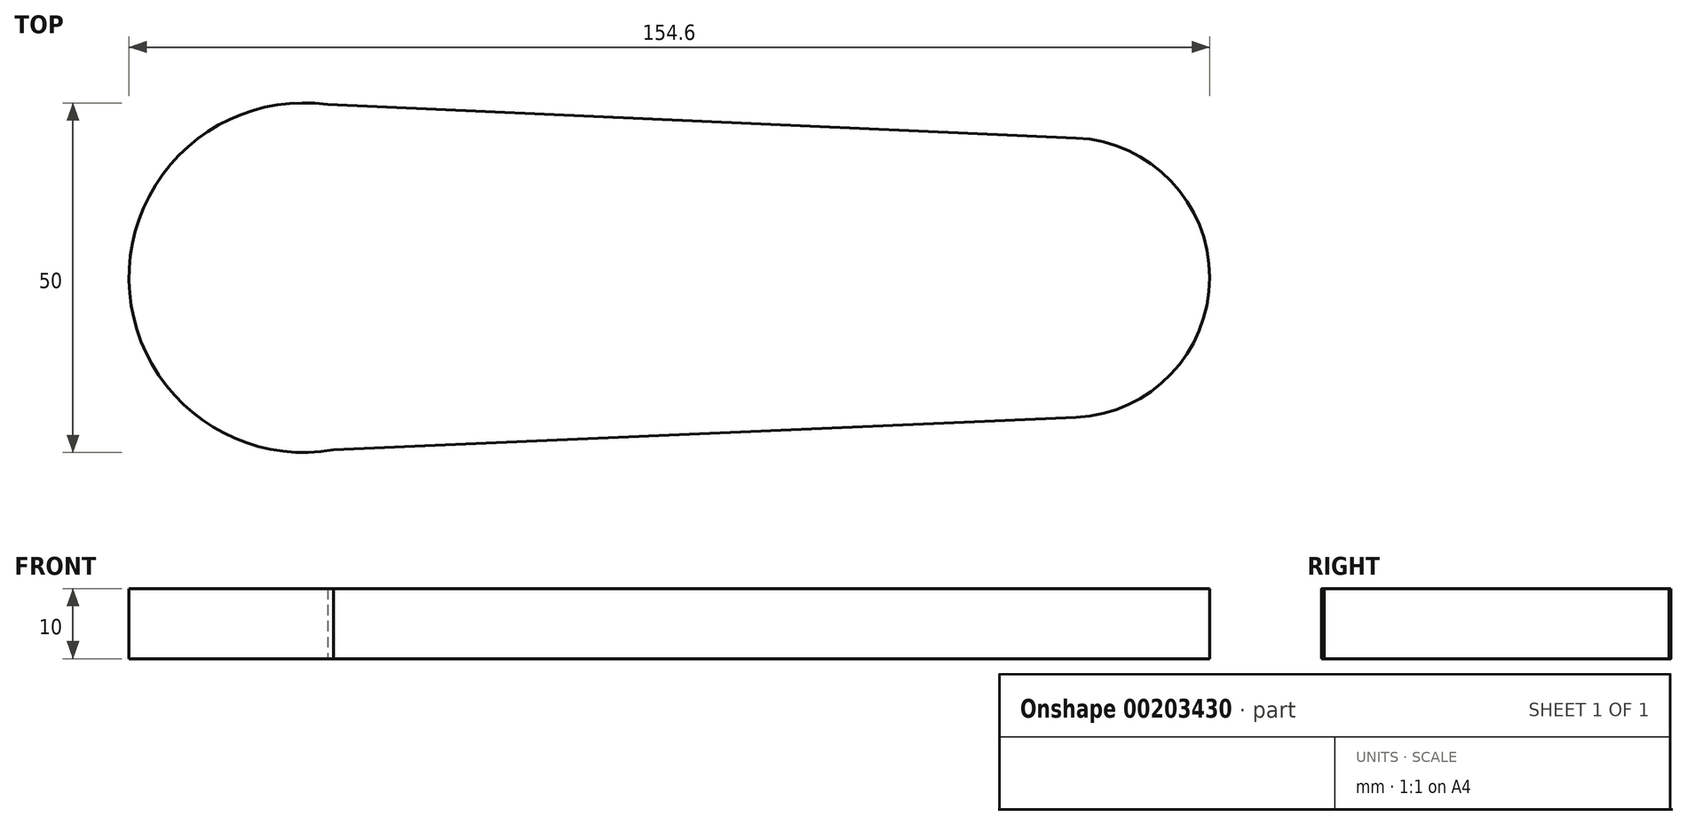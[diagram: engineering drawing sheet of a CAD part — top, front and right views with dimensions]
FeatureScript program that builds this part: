
annotation { "Feature Type Name" : "Feature", "Feature Type Description" : "" }
export const myFeature = defineFeature(function(context is Context, id is Id, definition is map)
    precondition{}
    {
        {
            var Q0;
            Q0=qCreatedBy(makeId("Top.planeOp"),FACE);
            var sketch = newSketch(context, id + "F0", { "sketchPlane" : qUnion([Q0])});
            skCircle(sketch, "E0", {"center": v(0, 0) * mm, "radius": 25 * mm});
            skCircle(sketch, "E1", {"center": v(109.6, 0) * mm, "radius": 20 * mm});
            skLineSegment(sketch, "E2", {"start": v(0, 0) * mm, "end": v(109.6, 0) * mm});
            skLineSegment(sketch, "E3", {"start": v(3.44, 24.76) * mm, "end": v(110.5, 19.98) * mm});
            skLineSegment(sketch, "E4", {"start": v(4.27, -24.63) * mm, "end": v(110.48, -19.98) * mm});
            skSolve(sketch);
        }
        {
            var Q0;
            {var subQ0=sQuery(id+"F0.wireOp",EDGE,"E0");var subQ1=makeQuery(id+"F0.imprint","INTERSECT",VERTEX,{"derivedFrom":[subQ0,sQuery(id+"F0.wireOp",EDGE,"E3")]});Q0=makeQuery(id+"F0.imprint","IMPRINT",FACE,{"disambiguationData":[TD([[makeQuery(id+"F0.imprint","IMPRINT",EDGE,{"disambiguationData":[TD([[subQ1,1.0]])],"derivedFrom":subQ0}),1.0]])]});}
            var Q1;
            {var subQ0=sQuery(id+"F0.wireOp",EDGE,"E1");var subQ1=makeQuery(id+"F0.imprint","INTERSECT",VERTEX,{"derivedFrom":[subQ0,sQuery(id+"F0.wireOp",EDGE,"E3")]});Q1=makeQuery(id+"F0.imprint","IMPRINT",FACE,{"disambiguationData":[TD([[makeQuery(id+"F0.imprint","IMPRINT",EDGE,{"disambiguationData":[TD([[subQ1,-1.0]])],"derivedFrom":subQ0}),1.0]])]});}
            var Q2;
            {var subQ0=sQuery(id+"F0.wireOp",EDGE,"E4");Q2=makeQuery(id+"F0.imprint","IMPRINT",FACE,{"disambiguationData":[TD([[makeQuery(id+"F0.imprint","IMPRINT",EDGE,{"derivedFrom":subQ0}),1.0]])]});}
            var Q3;
            {var subQ0=sQuery(id+"F0.wireOp",EDGE,"E3");Q3=makeQuery(id+"F0.imprint","IMPRINT",FACE,{"disambiguationData":[TD([[makeQuery(id+"F0.imprint","IMPRINT",EDGE,{"derivedFrom":subQ0}),-1.0]])]});}
            extrude(context, id + "F1", {"entities" : qUnion([Q0, Q1, Q2, Q3]), "depth" : 10 * mm});
        }
        {
            var Q0;
            Q0=qCreatedBy(makeId("Top.planeOp"),FACE);
            var sketch = newSketch(context, id + "F2", { "sketchPlane" : qUnion([Q0])});
            skCircle(sketch, "E5", {"center": v(0, 0) * mm, "radius": 21.1 * mm});
            skSolve(sketch);
        }
        {
            var Q0;
            Q0=sQuery(id+"F2.wireOp",EDGE,"E5");
            extrude(context, id + "F3", {"bodyType" : ToolBodyType.SURFACE, "surfaceEntities" : qUnion([Q0]), "depth" : 25 * mm});
        }
    });
